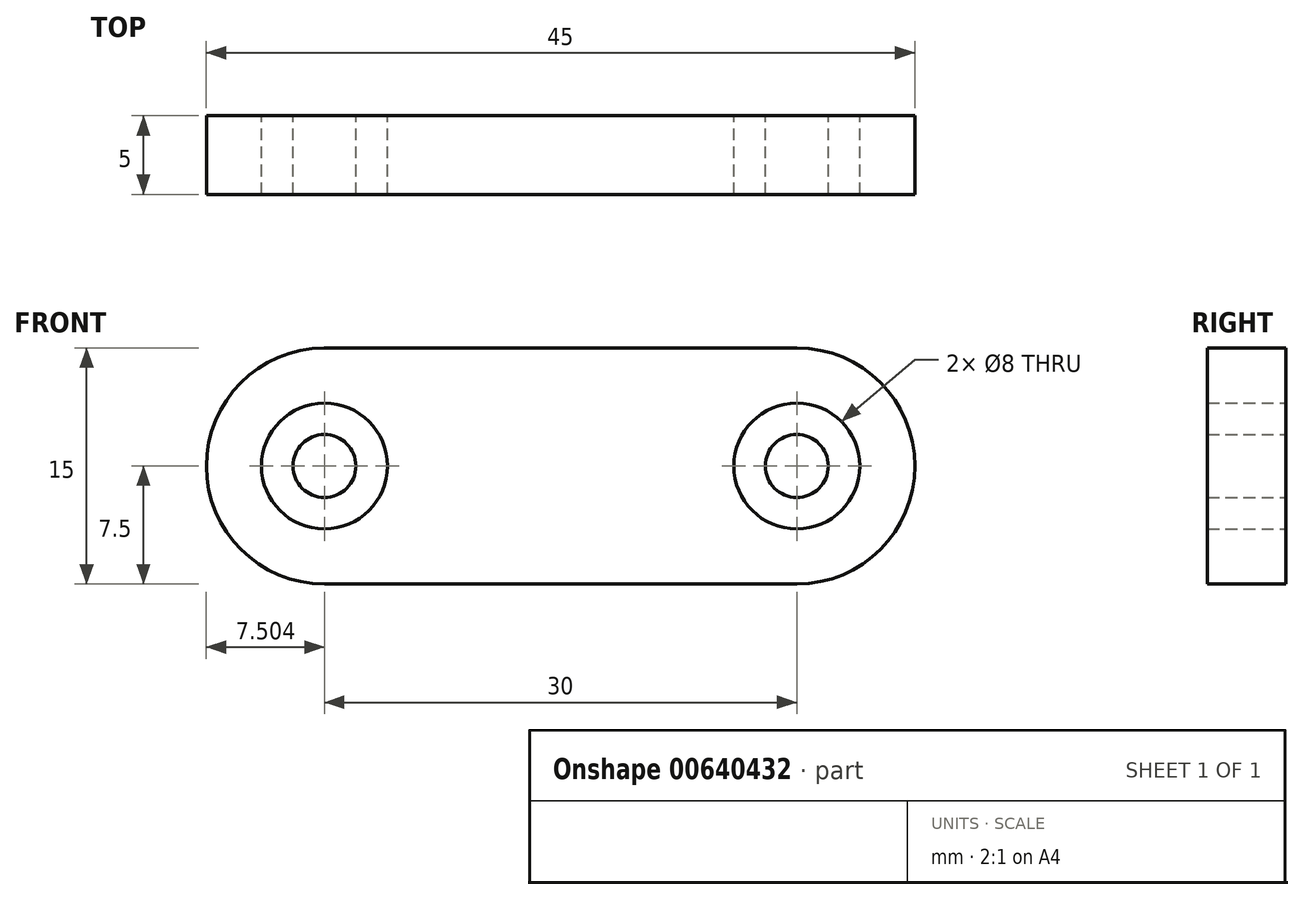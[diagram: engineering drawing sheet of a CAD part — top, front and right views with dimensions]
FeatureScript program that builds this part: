
annotation { "Feature Type Name" : "Feature", "Feature Type Description" : "" }
export const myFeature = defineFeature(function(context is Context, id is Id, definition is map)
    precondition{}
    {
        {
            var Q0;
            Q0=qCreatedBy(makeId("Front.planeOp"),FACE);
            var sketch = newSketch(context, id + "F0", { "sketchPlane" : qUnion([Q0])});
            skArc(sketch, "E0", {"start": v(-33.8, 7.5) * mm, "mid": v(-33.83, 7.5) * mm, "end": v(-33.86, 7.5) * mm});
            skArc(sketch, "E1", {"start": v(-3.83, -7.5) * mm, "mid": v(3.67, 0) * mm, "end": v(-3.83, 7.5) * mm});
            skLineSegment(sketch, "E2", {"start": v(-51.67, 0) * mm, "end": v(48.06, 0) * mm, "construction": true});
            skLineSegment(sketch, "E3", {"start": v(-33.86, 7.5) * mm, "end": v(-3.83, 7.5) * mm});
            skArc(sketch, "E4", {"start": v(-33.8, 7.5) * mm, "mid": v(-41.33, 0.02) * mm, "end": v(-33.83, -7.5) * mm});
            skLineSegment(sketch, "E5", {"start": v(-33.83, -7.5) * mm, "end": v(-3.83, -7.5) * mm});
            skCircle(sketch, "E6", {"center": v(-33.83, 0) * mm, "radius": 4 * mm});
            skCircle(sketch, "E7", {"center": v(-3.83, 0) * mm, "radius": 4 * mm});
            skCircle(sketch, "E8", {"center": v(-33.83, 0) * mm, "radius": 2 * mm});
            skCircle(sketch, "E9", {"center": v(-3.83, 0) * mm, "radius": 2 * mm});
            skSolve(sketch);
        }
        {
            var Q0;
            Q0=makeQuery(id+"F0.imprint","IMPRINT",FACE,{"disambiguationData":[TD([[makeQuery(id+"F0.imprint","IMPRINT",EDGE,{"derivedFrom":sQuery(id+"F0.wireOp",EDGE,"E1")}),1.0]])]});
            var Q1;
            Q1=makeQuery(id+"F0.imprint","IMPRINT",FACE,{"disambiguationData":[TD([[makeQuery(id+"F0.imprint","IMPRINT",EDGE,{"derivedFrom":sQuery(id+"F0.wireOp",EDGE,"E8")}),1.0]])]});
            var Q2;
            Q2=makeQuery(id+"F0.imprint","IMPRINT",FACE,{"disambiguationData":[TD([[makeQuery(id+"F0.imprint","IMPRINT",EDGE,{"derivedFrom":sQuery(id+"F0.wireOp",EDGE,"E9")}),1.0]])]});
            extrude(context, id + "F1", {"entities" : qUnion([Q0, Q1, Q2]), "endBound" : BoundingType.SYMMETRIC, "depth" : 5 * mm, "offsetDistance" : 25 * mm});
        }
    });
